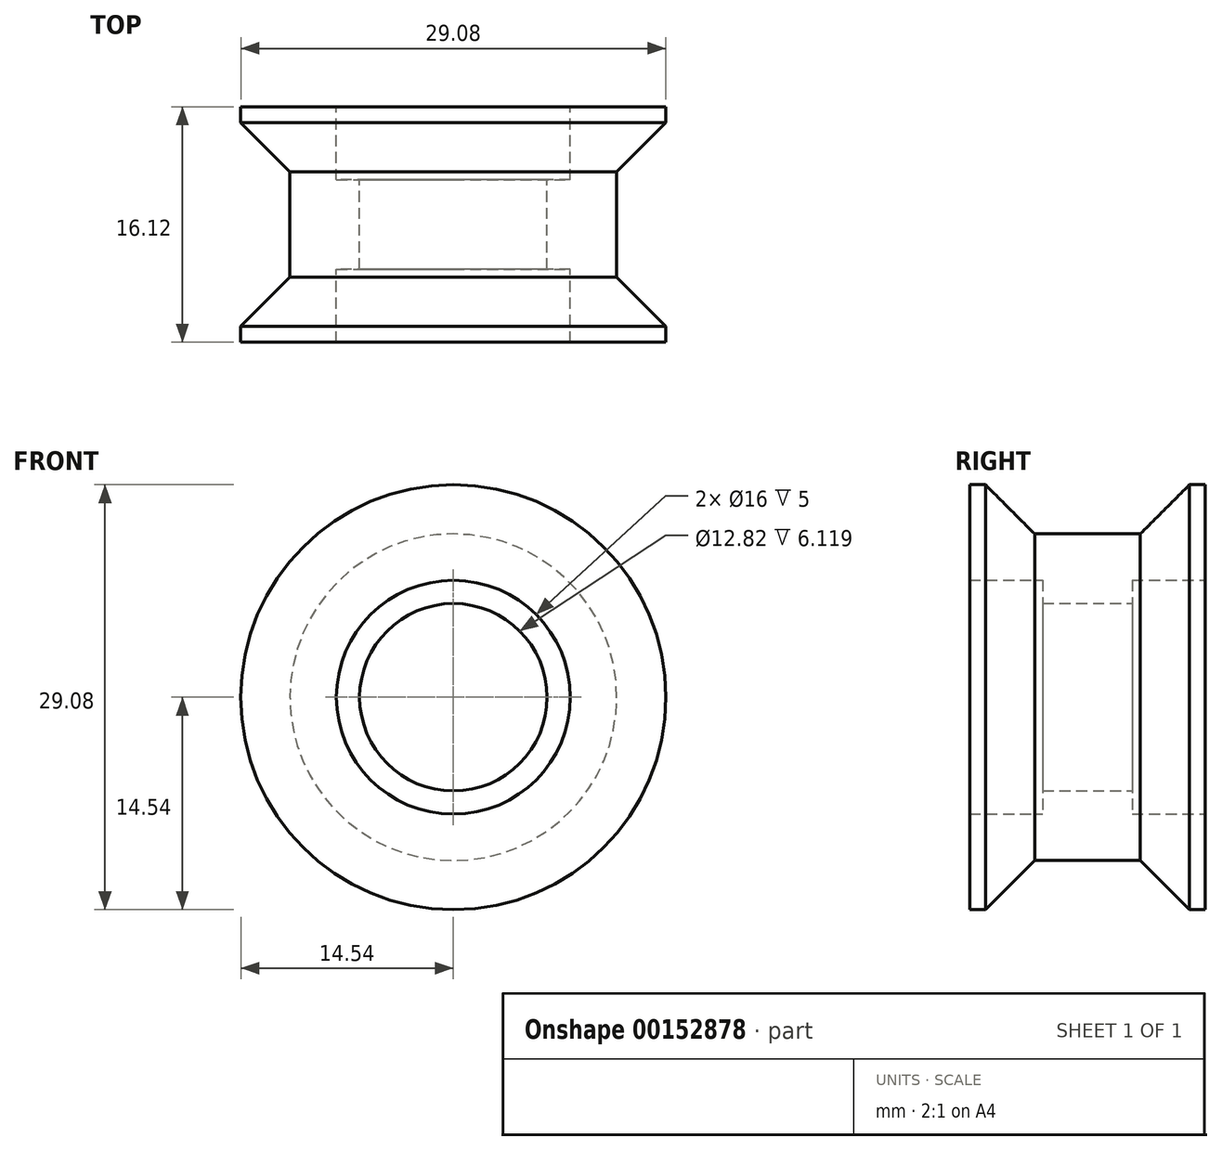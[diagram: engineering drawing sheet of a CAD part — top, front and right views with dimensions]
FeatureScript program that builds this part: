
annotation { "Feature Type Name" : "Feature", "Feature Type Description" : "" }
export const myFeature = defineFeature(function(context is Context, id is Id, definition is map)
    precondition{}
    {
        {
            var Q0;
            Q0=qCreatedBy(makeId("Top.planeOp"),FACE);
            var sketch = newSketch(context, id + "F0", { "sketchPlane" : qUnion([Q0])});
            skLineSegment(sketch, "E0", {"start": v(-14.54, 0) * mm, "end": v(-14.54, 1.08) * mm});
            skLineSegment(sketch, "E1", {"start": v(-14.54, 1.08) * mm, "end": v(-11.18, 4.45) * mm});
            skLineSegment(sketch, "E2", {"start": v(-11.18, 4.45) * mm, "end": v(-11.18, 11.67) * mm});
            skLineSegment(sketch, "E3", {"start": v(-11.18, 11.67) * mm, "end": v(-14.54, 15.04) * mm});
            skLineSegment(sketch, "E4", {"start": v(-14.54, 15.04) * mm, "end": v(-14.54, 16.12) * mm});
            skLineSegment(sketch, "E5", {"start": v(-14.54, 16.12) * mm, "end": v(-8, 16.12) * mm});
            skLineSegment(sketch, "E6.bottom", {"start": v(0, 0) * mm, "end": v(-8, 0) * mm, "construction": true});
            skLineSegment(sketch, "E6.top", {"start": v(0, 16.12) * mm, "end": v(-8, 16.12) * mm, "construction": true});
            skLineSegment(sketch, "E6.left", {"start": v(0, 0) * mm, "end": v(0, 16.12) * mm, "construction": true});
            skLineSegment(sketch, "E7", {"start": v(-8, 0) * mm, "end": v(-14.54, 0) * mm});
            skLineSegment(sketch, "E8", {"start": v(-14.54, 1.08) * mm, "end": v(-14.54, 15.04) * mm, "construction": true});
            skLineSegment(sketch, "E9", {"start": v(-14.54, 8.06) * mm, "end": v(-11.18, 8.06) * mm, "construction": true});
            skLineSegment(sketch, "E10", {"start": v(-11.18, 8.06) * mm, "end": v(-8, 8.06) * mm, "construction": true});
            skLineSegment(sketch, "E11.bottom", {"start": v(-8, 11.12) * mm, "end": v(-6.41, 11.12) * mm});
            skLineSegment(sketch, "E11.top", {"start": v(-8, 5) * mm, "end": v(-6.41, 5) * mm});
            skLineSegment(sketch, "E11.left", {"start": v(-8, 11.12) * mm, "end": v(-8, 5) * mm, "construction": true});
            skLineSegment(sketch, "E11.right", {"start": v(-6.41, 11.12) * mm, "end": v(-6.41, 5) * mm});
            skLineSegment(sketch, "E12", {"start": v(-8, 0) * mm, "end": v(-8, 5) * mm});
            skLineSegment(sketch, "E13", {"start": v(-8, 16.12) * mm, "end": v(-8, 11.12) * mm});
            skSolve(sketch);
        }
        {
            var Q0;
            Q0=qCreatedBy(makeId("Front.planeOp"),FACE);
            var sketch = newSketch(context, id + "F1", { "sketchPlane" : qUnion([Q0])});
            skCircle(sketch, "E14", {"center": v(0, 0) * mm, "radius": 1.59 * mm});
            skSolve(sketch);
        }
        {
            var Q0;
            Q0=makeQuery(id+"F0.imprint","IMPRINT",FACE,{"disambiguationData":[TD([[makeQuery(id+"F0.imprint","IMPRINT",EDGE,{"derivedFrom":sQuery(id+"F0.wireOp",EDGE,"E0")}),-1.0]])]});
            var Q1;
            Q1=sQuery(id+"F1.wireOp",EDGE,"E14");
            revolve(context, id + "F2", {"entities" : qUnion([Q0]), "axis" : qUnion([Q1]), "revolveType" : RevolveType.FULL});
        }
    });
